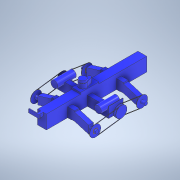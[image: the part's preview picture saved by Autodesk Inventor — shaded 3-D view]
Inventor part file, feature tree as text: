
AUTODESK INVENTOR PART (.ipt)
format: ipt  version: 2021 (Build 250183000, 183)  size: 748,032 bytes
history: native  units: mm
features: extrude x38, sketch x36, projected_geometry x15, plane x7
ambient origin geometry x8: Origin, YZ Plane, XZ Plane, XY Plane, X Axis, Y Axis, Z Axis, Center Point
bodies: Body1 (feature_tree)
feature tree (96):
  plane  "Work Plane1"
  extrude  "Extrusion1"  Depth=3.0mm
  extrude  "Extrusion2"  Depth=115.4mm TaperAngle=0.0deg
  extrude  "Extrusion3"  Depth=78.5mm TaperAngle=0.0deg
  extrude  "Extrusion4"  Depth=70.0mm
  extrude  "Extrusion5"  Depth=115.4mm
  extrude  "Extrusion6"  Depth=10.0mm
  extrude  "Extrusion7"  Depth=115.4mm TaperAngle=0.0deg
  extrude  "Extrusion8"  Depth=13.941mm TaperAngle=0.0deg
  extrude  "Extrusion9"  Depth=5.5mm
  extrude  "Extrusion10"  Depth=7.0mm TaperAngle=0.0deg
  extrude  "Extrusion11"  Depth=40.0mm
  extrude  "Extrusion12"  Depth=40.0mm TaperAngle=0.0deg
  extrude  "Extrusion13"  Depth=130.0mm
  extrude  "Extrusion14"  Depth=20.0mm TaperAngle=0.0deg
  extrude  "Extrusion15"  Depth=125.0mm
  sketch  "Sketch18"  dims[d61=3.0mm d62=0.0mm d64=30.0mm]
  extrude  "Extrusion16"  Depth=30.0mm
  extrude  "Extrusion17"  Depth=100.0mm TaperAngle=0.0deg
  extrude  "Extrusion18"  Depth=3.0mm TaperAngle=0.0deg
  extrude  "Extrusion19"  Depth=3.0mm TaperAngle=0.0deg
  sketch  "Sketch21"  dims[d73=30.0mm d74=3.0mm d75=0.0mm]
  extrude  "Extrusion20"  Depth=30.0mm
  extrude  "Extrusion21"  Depth=30.0mm
  extrude  "Extrusion22"  TaperAngle=0.0deg  [1 undecoded]
  extrude  "Extrusion23"  Depth=30.0mm
  extrude  "Extrusion24"  [1 undecoded]
  plane  "Work Plane2"
  plane  "Work Plane3"
  extrude  "Extrusion25"  Depth=95.0mm
  extrude  "Extrusion26"  Depth=95.0mm
  plane  "Work Plane4"
  extrude  "Extrusion27"  Depth=3.0mm TaperAngle=0.0deg
  plane  "Work Plane5"
  extrude  "Extrusion28"  Depth=95.0mm
  extrude  "Extrusion29"  [1 undecoded]
  plane  "Work Plane6"
  extrude  "Extrusion30"  Depth=3.0mm TaperAngle=0.0deg
  extrude  "Extrusion31"  Depth=3.0mm TaperAngle=0.0deg
  extrude  "Extrusion32"  Depth=95.0mm
  plane  "Work Plane7"
  extrude  "Extrusion33"  Depth=3.0mm TaperAngle=0.0deg
  extrude  "Extrusion34"  [1 undecoded]
  extrude  "Extrusion35"  Depth=35.0mm TaperAngle=0.0deg
  extrude  "Extrusion36"  Depth=35.0mm TaperAngle=0.0deg
  extrude  "Extrusion37"  Depth=2.5mm
  extrude  "Extrusion38"  Depth=2.5mm
  sketch  "Sketch1"  dims[d1=3.0mm d2=0.0mm d4=37.7mm]
  sketch  "Sketch2"  dims[d5=75.4mm d6=115.4mm d7=0.0mm]
  sketch  "Sketch3"  dims[d12=40.0mm d13=78.5mm d14=0.0mm]
  sketch  "Sketch4"  dims[d15=35.0mm d16=70.0mm]
  sketch  "Sketch5"  dims[d17=115.4mm d18=0.0mm d19=98.5mm]
  sketch  "Sketch6"  dims[d20=197.0mm d24=10.0mm]
  projected_geometry  "Projected Loop2"
  projected_geometry  "Projected Loop3"
  sketch  "Sketch8"  dims[d26=115.4mm d27=0.0mm d28=115.4mm d29=0.0mm]
  sketch  "Sketch9"  dims[d30=50.0mm d31=13.941mm d32=0.0mm]
  sketch  "Sketch10"  dims[d37=30.0mm d38=0.0mm d39=5.5mm]
  sketch  "Sketch11"  dims[d40=93.5mm d41=7.0mm d42=0.0mm]
  projected_geometry  "Projected Loop4"
  projected_geometry  "Projected Loop5"
  projected_geometry  "Projected Loop6"
  projected_geometry  "Projected Loop7"
  projected_geometry  "Projected Loop8"
  sketch  "Sketch13"  dims[d43=10.0mm d44=0.0mm d45=40.0mm]
  sketch  "Sketch14"  dims[d46=10.0mm d47=0.0mm d51=40.0mm d52=0.0mm]
  sketch  "Sketch15"  dims[d53=20.0mm d54=0.0mm d55=130.0mm]
  sketch  "Sketch16"  dims[d56=40.0mm d57=20.0mm d58=0.0mm]
  sketch  "Sketch17"  dims[d59=90.0mm d60=125.0mm]
  sketch  "Sketch19"  dims[d65=60.0mm d66=0.0mm d67=100.0mm d68=0.0mm]
  projected_geometry  "Projected Loop9"
  sketch  "Sketch20"  dims[d69=100.0mm d70=0.0mm d71=3.0mm d72=0.0mm]
  projected_geometry  "Projected Loop10"
  sketch  "Sketch22"  dims[d76=3.0mm d77=0.0mm d78=30.0mm]
  sketch  "Sketch23"  dims[d79=50.5mm d80=0.0mm d81=30.0mm]
  sketch  "Sketch24"  dims[d82=30.0mm d83=0.0mm]
  sketch  "Sketch25"  dims[d84=30.0mm d85=30.0mm]
  sketch  "Sketch26"  dims[d86=50.5mm d87=0.0mm d88=-15.0mm]
  sketch  "Sketch27"  dims[d89=-15.0mm d90=95.0mm]
  sketch  "Sketch28"  dims[d91=3.0mm d92=0.0mm d93=95.0mm]
  sketch  "Sketch29"  dims[d94=95.0mm d95=3.0mm d96=0.0mm]
  sketch  "Sketch30"  dims[d97=-35.0mm d98=95.0mm]
  sketch  "Sketch31"  dims[d99=3.0mm d100=0.0mm d101=-35.0mm]
  sketch  "Sketch32"  dims[d102=95.0mm d103=3.0mm d104=0.0mm]
  sketch  "Sketch33"  dims[d108=25.0mm d109=3.0mm d110=0.0mm]
  sketch  "Sketch34"  dims[d111=-17.0mm d112=95.0mm]
  sketch  "Sketch35"  dims[d113=3.0mm d114=0.0mm d115=3.0mm d116=0.0mm]
  projected_geometry  "Projected Loop11"
  projected_geometry  "Projected Loop12"
  sketch  "Sketch36"  dims[d117=35.5mm d118=0.0mm d119=-17.0mm]
  projected_geometry  "Projected Loop13"
  projected_geometry  "Projected Loop14"
  sketch  "Sketch37"  dims[d120=95.0mm d121=35.0mm d122=0.0mm]
  projected_geometry  "Projected Loop15"
  sketch  "Sketch38"  dims[d123=95.0mm d124=35.0mm d125=0.0mm d126=2.5mm d127=2.5mm d128=35.0mm d129=0.0mm d130=2.5mm d131=2.5mm d132=2.5mm d133=35.0mm d134=0.0mm d135=35.0mm d136=0.0mm d137=35.0mm d138=0.0mm]
  projected_geometry  "Projected Loop16"
note: 4 required parameter values undecoded (feature->parameter linkage not recoverable at this tier; creation-order binding heuristic only, values carry confidence <= 0.55)
